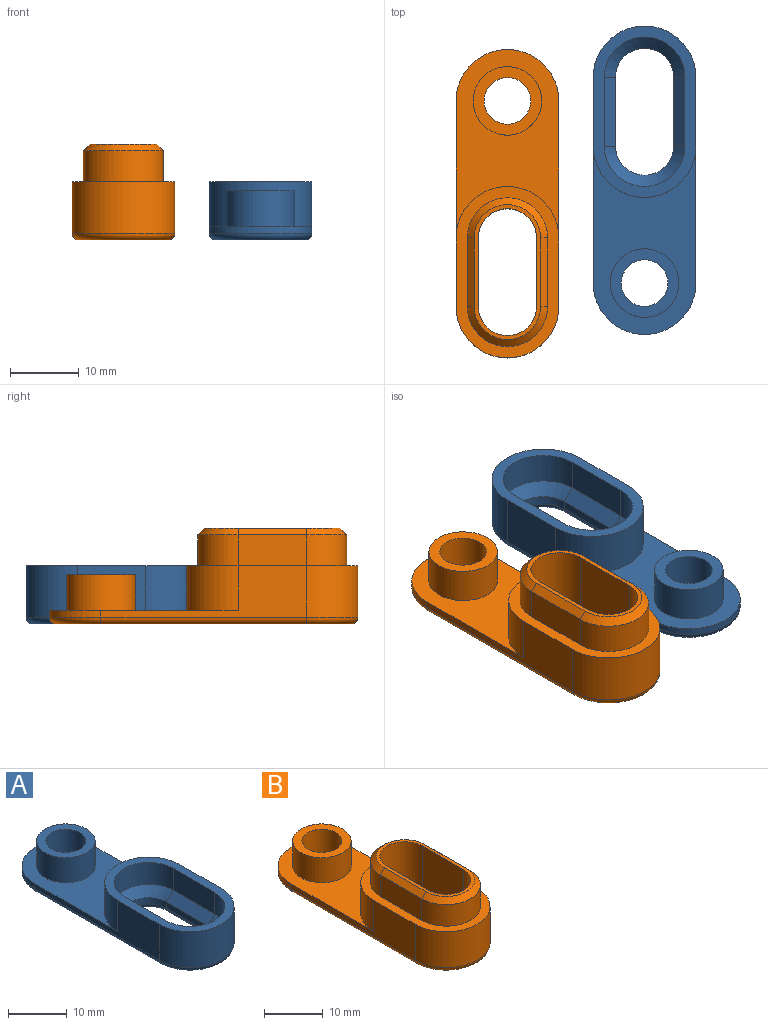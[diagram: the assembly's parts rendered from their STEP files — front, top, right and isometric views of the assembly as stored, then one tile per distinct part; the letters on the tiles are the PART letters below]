
ASSEMBLY  parts=2 mates=1
PART A: 32 faces, bbox 16.2x46.2x8.5 mm
  f0: plane 27.5x15mm, normal (0,0,1), area 221.5mm2, adj f4,f6,f8,f11,f16
  f1: cylinder r=4.25mm len=8.5mm, axis (0,0,1), area 17.4mm2, adj f2,f9,f19,f27
  f2: plane 10x1.3mm, normal (-1,0,0), area 13mm2, adj f1,f3,f21,f29
  f3: cylinder r=4.25mm len=8.5mm, axis (0,0,1), area 17.4mm2, adj f2,f9,f22,f30
  f4: plane 30x7.5mm, normal (-1,0,0), area 95mm2, adj f0,f5,f8,f16,f18,f26
  f5: cylinder r=7.5mm len=15mm, axis (0,0,1), area 176.7mm2, adj f4,f6,f18,f24
  f6: plane 30x7.5mm, normal (1,0,0), area 95mm2, adj f0,f5,f8,f16,f18,f23
  f7: cylinder r=3.4mm len=6.8mm, axis (0,0,1), area 132.4mm2, adj f12,f31
  f8: cylinder r=7.5mm len=15mm, axis (0,0,1), area 23.6mm2, adj f0,f4,f6,f25
  f9: plane 10x1.3mm, normal (1,0,0), area 13mm2, adj f1,f3,f20,f28
  f10: plane 43x13mm, normal (0,0,-1), area 270.3mm2, adj f23,f24,f25,f26,f27,f28,f29,f30
  f11: cylinder r=5mm len=10mm, axis (0,0,-1), area 163.4mm2, adj f0,f12
  f12: plane 10x10mm, normal (0,0,1), area 42.2mm2, adj f7,f11
  f13: cylinder r=5.9mm len=11.8mm, axis (0,0,-1), area 84.3mm2, adj f14,f17,f18,f19
  f14: plane 10x4.55mm, normal (-1,0,0), area 45.5mm2, adj f13,f15,f18,f21
  f15: cylinder r=5.9mm len=11.8mm, axis (0,0,-1), area 84.3mm2, adj f14,f17,f18,f22
  f16: cylinder r=7.5mm len=15mm, axis (0,0,-1), area 153.2mm2, adj f0,f4,f6,f18
  f17: plane 10x4.55mm, normal (1,0,0), area 45.5mm2, adj f13,f15,f18,f20
  f18: plane 25x15mm, normal (0,0,1), area 99.4mm2, adj f4,f5,f6,f13,f14,f15,f16,f17
  f19: cone r=4.25mm half-angle=45deg, axis (0,0,1), area 37.2mm2, adj f1,f13,f20,f21
  f20: plane 10x1.65mm, normal (0.71,0,0.71), area 23.3mm2, adj f9,f17,f19,f22
  f21: plane 10x1.65mm, normal (-0.71,0,0.71), area 23.3mm2, adj f2,f14,f19,f22
  f22: cone r=4.25mm half-angle=45deg, axis (0,0,1), area 37.2mm2, adj f3,f15,f20,f21
  f23: cylinder r=1mm len=30mm, axis (0,-1,0), area 47.1mm2, adj f6,f10,f24,f25
  f24: torus R=6.5mm, axis (0,0,1), area 35.2mm2, adj f5,f10,f23,f26
  f25: torus R=6.5mm, axis (0,0,1), area 35.2mm2, adj f8,f10,f23,f26
  f26: cylinder r=1mm len=30mm, axis (0,1,0), area 47.1mm2, adj f4,f10,f24,f25
  f27: torus R=5.25mm, axis (0,0,1), area 22.8mm2, adj f1,f10,f28,f29
  f28: cylinder r=1mm len=10mm, axis (0,-1,0), area 15.7mm2, adj f9,f10,f27,f30
  f29: cylinder r=1mm len=10mm, axis (0,1,0), area 15.7mm2, adj f2,f10,f27,f30
  f30: torus R=5.25mm, axis (0,0,1), area 22.8mm2, adj f3,f10,f28,f29
  f31: torus R=4.4mm, axis (0,0,1), area 37.1mm2, adj f7,f10
PART B: 33 faces, bbox 16.2x46.2x14 mm
  f0: plane 27.5x15mm, normal (0,0,1), area 221.5mm2, adj f4,f5,f6,f11,f13
  f1: cylinder r=4.25mm len=13mm, axis (0,0,1), area 173.6mm2, adj f2,f9,f19,f20
  f2: plane 13x10mm, normal (1,0,0), area 130mm2, adj f1,f3,f19,f22
  f3: cylinder r=4.25mm len=13mm, axis (0,0,1), area 173.6mm2, adj f2,f9,f19,f23
  f4: plane 30x7.5mm, normal (1,0,0), area 95mm2, adj f0,f5,f8,f13,f14,f27
  f5: cylinder r=7.5mm len=15mm, axis (0,0,1), area 23.6mm2, adj f0,f4,f6,f25
  f6: plane 30x7.5mm, normal (-1,0,0), area 95mm2, adj f0,f5,f8,f13,f14,f26
  f7: cylinder r=3.4mm len=6.8mm, axis (0,0,1), area 132.4mm2, adj f12,f24
  f8: cylinder r=7.5mm len=15mm, axis (0,0,1), area 176.7mm2, adj f4,f6,f14,f28
  f9: plane 13x10mm, normal (-1,0,0), area 130mm2, adj f1,f3,f19,f21
  f10: plane 43x13mm, normal (0,0,-1), area 270.3mm2, adj f20,f21,f22,f23,f24,f25,f26,f27
  f11: cylinder r=5mm len=10mm, axis (0,0,-1), area 163.4mm2, adj f0,f12
  f12: plane 10x10mm, normal (0,0,1), area 42.2mm2, adj f7,f11
  f13: cylinder r=7.5mm len=15mm, axis (0,0,-1), area 153.2mm2, adj f0,f4,f6,f14
  f14: plane 25x15mm, normal (0,0,1), area 102.2mm2, adj f4,f6,f8,f13,f15,f16,f17,f18
  f15: cylinder r=5.85mm len=11.7mm, axis (0,0,-1), area 82.7mm2, adj f14,f16,f18,f32
  f16: plane 10x4.5mm, normal (-1,0,0), area 45mm2, adj f14,f15,f17,f31
  f17: cylinder r=5.85mm len=11.7mm, axis (0,0,-1), area 82.7mm2, adj f14,f16,f18,f29
  f18: plane 10x4.5mm, normal (1,0,0), area 45mm2, adj f14,f15,f17,f30
  f19: plane 19.7x9.7mm, normal (0,0,1), area 29.2mm2, adj f1,f2,f3,f9,f29,f30,f31,f32
  f20: torus R=5.25mm, axis (0,0,1), area 22.8mm2, adj f1,f10,f21,f22
  f21: cylinder r=1mm len=10mm, axis (0,1,0), area 15.7mm2, adj f9,f10,f20,f23
  f22: cylinder r=1mm len=10mm, axis (0,-1,0), area 15.7mm2, adj f2,f10,f20,f23
  f23: torus R=5.25mm, axis (0,0,1), area 22.8mm2, adj f3,f10,f21,f22
  f24: torus R=4.4mm, axis (0,0,1), area 37.1mm2, adj f7,f10
  f25: torus R=6.5mm, axis (0,0,1), area 35.2mm2, adj f5,f10,f26,f27
  f26: cylinder r=1mm len=30mm, axis (0,1,0), area 47.1mm2, adj f6,f10,f25,f28
  f27: cylinder r=1mm len=30mm, axis (0,-1,0), area 47.1mm2, adj f4,f10,f25,f28
  f28: torus R=6.5mm, axis (0,0,1), area 35.2mm2, adj f8,f10,f26,f27
  f29: cone r=4.85mm half-angle=45deg, axis (0,0,-1), area 23.8mm2, adj f17,f19,f30,f31
  f30: plane 10x1mm, normal (0.71,0,0.71), area 14.1mm2, adj f18,f19,f29,f32
  f31: plane 10x1mm, normal (-0.71,0,0.71), area 14.1mm2, adj f16,f19,f29,f32
  f32: cone r=4.85mm half-angle=45deg, axis (0,0,-1), area 23.8mm2, adj f15,f19,f30,f31
PLACE A rot(axis=(0,0,1),180deg) t=(27.4,-5.17,-3.01)mm
PLACE B t=(7.4,21.41,-3.01)mm
MATE planar A.f10 <-> B.f10  axis (0,0,-1) through (27.4,6.12,-5.01)mm
